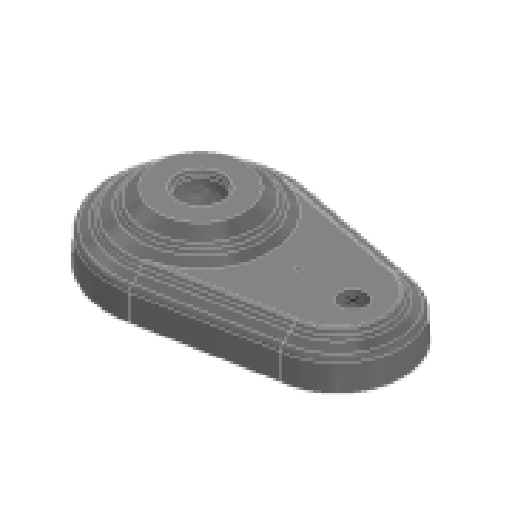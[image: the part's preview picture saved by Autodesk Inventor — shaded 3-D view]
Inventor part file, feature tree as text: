
AUTODESK INVENTOR PART (.ipt)
format: ipt  version: 2024.3 (Build 283343000, 343)  size: 191,488 bytes
history: native  units: in
note: dims shown in document units (in); Inventor stores cm internally (conversion verified against a paired STEP export)
features: sketch x4, other x1, extrude x1
ambient origin geometry x8: Origin, YZ Plane, XZ Plane, XY Plane, X Axis, Y Axis, Z Axis, Center Point
bodies: Solid1 (feature_tree)
feature tree (6):
  other  "Adjustable feet for ground mounting LV.FO-60-14+SJF-M6 (0)-1"
  sketch  "Sketch1"  dims[d0=0.3346in d1=0.0in d2=0.0in]
  sketch  "Sketch2"
  sketch  "Sketch3"
  extrude  "Extrusion1"  TaperAngle=0.0deg  [1 undecoded]
  sketch  "Sketch4"
note: 1 required parameter value undecoded (feature->parameter linkage not recoverable at this tier; creation-order binding heuristic only, values carry confidence <= 0.55)
